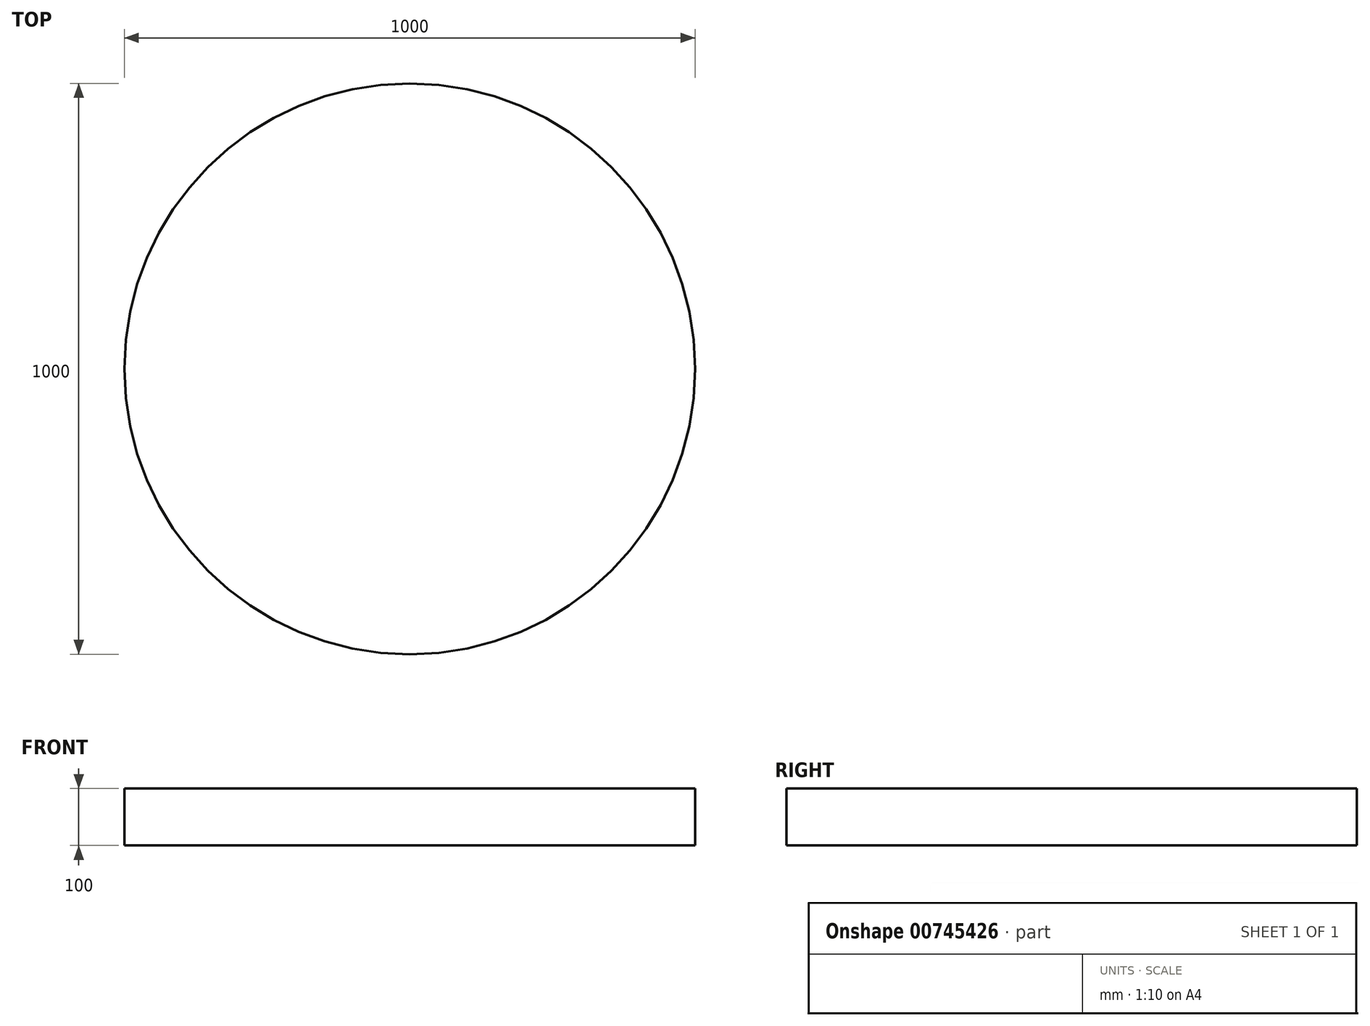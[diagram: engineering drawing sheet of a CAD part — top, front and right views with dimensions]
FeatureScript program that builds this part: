
annotation { "Feature Type Name" : "Feature", "Feature Type Description" : "" }
export const myFeature = defineFeature(function(context is Context, id is Id, definition is map)
    precondition{}
    {
        {
            var Q0;
            Q0=qCreatedBy(makeId("Top.planeOp"),FACE);
            var sketch = newSketch(context, id + "F0", { "sketchPlane" : qUnion([Q0])});
            skCircle(sketch, "E0", {"center": v(0, 0) * mm, "radius": 500 * mm});
            skSolve(sketch);
        }
        {
            var Q0;
            Q0 = qSketchRegion(id + "F0", true);
            extrude(context, id + "F1", {"entities" : qUnion([Q0]), "depth" : 100 * mm, "offsetDistance" : 25 * mm});
        }
    });
